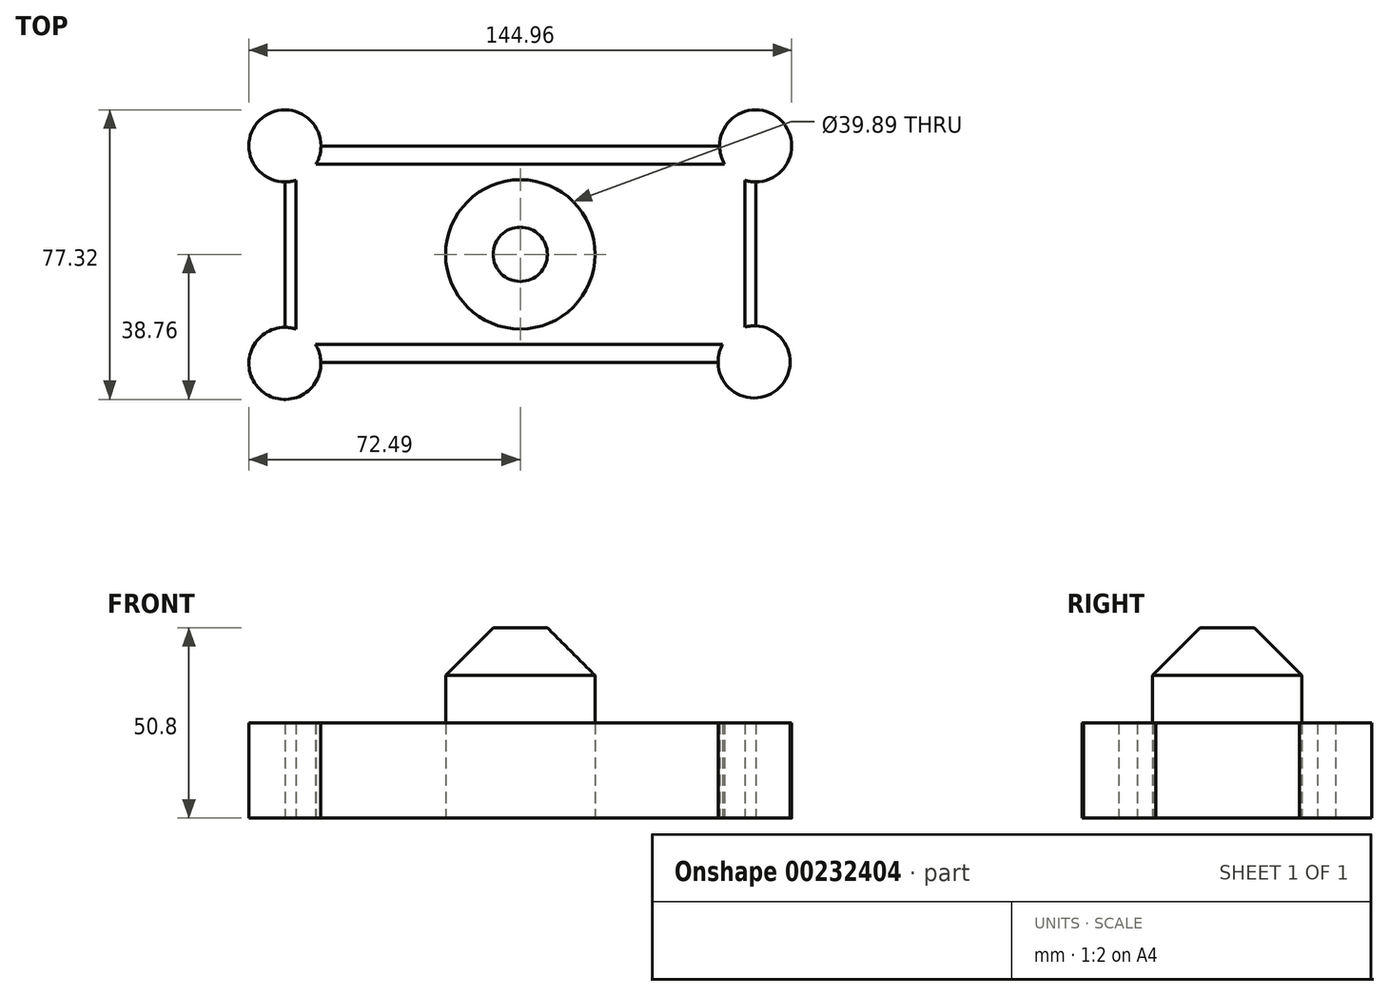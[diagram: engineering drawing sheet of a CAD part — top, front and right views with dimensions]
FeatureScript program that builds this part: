
annotation { "Feature Type Name" : "Feature", "Feature Type Description" : "" }
export const myFeature = defineFeature(function(context is Context, id is Id, definition is map)
    precondition{}
    {
        {
            var Q0;
            Q0=qCreatedBy(makeId("Top.planeOp"),FACE);
            var sketch = newSketch(context, id + "F0", { "sketchPlane" : qUnion([Q0])});
            skLineSegment(sketch, "E0.bottom", {"start": v(53.23, 28.94) * mm, "end": v(-53.23, 28.94) * mm});
            skLineSegment(sketch, "E0.top", {"start": v(52.82, -28.94) * mm, "end": v(-53.26, -28.94) * mm});
            skLineSegment(sketch, "E0.left", {"start": v(62.85, 19.32) * mm, "end": v(62.85, -19.13) * mm});
            skLineSegment(sketch, "E0.right", {"start": v(-62.85, 19.32) * mm, "end": v(-62.85, -19.52) * mm});
            skPoint(sketch, "E0.middle", {"position": v(0, 0) * mm});
            skCircle(sketch, "E1", {"center": v(0, 0) * mm, "radius": 19.94 * mm});
            skArc(sketch, "E2", {"start": v(-54.56, 24.06) * mm, "mid": v(-68.85, 36.46) * mm, "end": v(-59.92, 19.78) * mm});
            skCircle(sketch, "E3", {"center": v(62.85, 28.94) * mm, "radius": 9.62 * mm});
            skCircle(sketch, "E4", {"center": v(62.44, -28.74) * mm, "radius": 9.62 * mm});
            skCircle(sketch, "E5", {"center": v(-62.87, -29.14) * mm, "radius": 9.62 * mm});
            skLineSegment(sketch, "E6.bottom", {"start": v(-54.56, 24.06) * mm, "end": v(54.56, 24.06) * mm});
            skLineSegment(sketch, "E6.top", {"start": v(-54.7, -24.06) * mm, "end": v(54.03, -24.06) * mm});
            skLineSegment(sketch, "E6.left", {"start": v(-59.92, 19.78) * mm, "end": v(-59.92, -19.98) * mm});
            skLineSegment(sketch, "E6.right", {"start": v(59.92, 19.78) * mm, "end": v(59.92, -19.45) * mm});
            skPoint(sketch, "E7.orphan", {"position": v(59.92, 24.06) * mm});
            skPoint(sketch, "E8.orphan", {"position": v(62.85, -28.94) * mm});
            skPoint(sketch, "E9.orphan", {"position": v(-62.85, -28.94) * mm});
            skPoint(sketch, "E10.orphan", {"position": v(-59.92, 24.06) * mm});
            skPoint(sketch, "E11.orphan", {"position": v(-59.92, -24.06) * mm});
            skPoint(sketch, "E12.orphan", {"position": v(59.92, -24.06) * mm});
            skSolve(sketch);
        }
        {
            var Q0;
            {var subQ0=sQuery(id+"F0.wireOp",EDGE,"E0.right");Q0=makeQuery(id+"F0.imprint","IMPRINT",FACE,{"disambiguationData":[TD([[makeQuery(id+"F0.imprint","IMPRINT",EDGE,{"derivedFrom":subQ0}),1.0]])]});}
            var Q1;
            {var subQ0=sQuery(id+"F0.wireOp",EDGE,"E0.top");Q1=makeQuery(id+"F0.imprint","IMPRINT",FACE,{"disambiguationData":[TD([[makeQuery(id+"F0.imprint","IMPRINT",EDGE,{"derivedFrom":subQ0}),-1.0]])]});}
            var Q2;
            {var subQ0=sQuery(id+"F0.wireOp",EDGE,"E0.left");Q2=makeQuery(id+"F0.imprint","IMPRINT",FACE,{"disambiguationData":[TD([[makeQuery(id+"F0.imprint","IMPRINT",EDGE,{"derivedFrom":subQ0}),-1.0]])]});}
            var Q3;
            {var subQ0=sQuery(id+"F0.wireOp",EDGE,"E0.bottom");Q3=makeQuery(id+"F0.imprint","IMPRINT",FACE,{"disambiguationData":[TD([[makeQuery(id+"F0.imprint","IMPRINT",EDGE,{"derivedFrom":subQ0}),1.0]])]});}
            extrude(context, id + "F1", {"entities" : qUnion([Q0, Q1, Q2, Q3]), "depth" : 25.4 * mm});
        }
        {
            var Q0;
            Q0=makeQuery(id+"F0.imprint","IMPRINT",FACE,{"disambiguationData":[TD([[makeQuery(id+"F0.imprint","IMPRINT",EDGE,{"derivedFrom":sQuery(id+"F0.wireOp",EDGE,"E1")}),1.0]])]});
            extrude(context, id + "F2", {"entities" : qUnion([Q0]), "depth" : 50.8 * mm});
        }
        {
            var Q0;
            Q0=makeQuery(id+"F2.opExtrude","CAP_FACE",FACE,{"disambiguationData":[OSD([sQuery(id+"F0.wireOp",EDGE,"E1")])],"isStart":false});
            chamfer(context, id + "F3", {"entities" : qUnion([Q0]), "width" : 12.7 * mm, "tangentPropagation" : true});
        }
        {
            var Q0;
            {var subQ0=sQuery(id+"F0.wireOp",EDGE,"E4");var subQ1=makeQuery(id+"F0.imprint","INTERSECT",VERTEX,{"derivedFrom":[sQuery(id+"F0.wireOp",EDGE,"E0.left"),subQ0]});Q0=makeQuery(id+"F0.imprint","IMPRINT",FACE,{"disambiguationData":[TD([[makeQuery(id+"F0.imprint","IMPRINT",EDGE,{"disambiguationData":[TD([[subQ1,-1.0]])],"derivedFrom":subQ0}),1.0]])]});}
            var Q1;
            Q1 = qSketchRegion(id + "F0", true);
            extrude(context, id + "F4", {"entities" : qUnion([Q0, Q1]), "depth" : 25.4 * mm});
        }
    });
